# Revit family: RN 81124 Optipress-Aquaplus-Übergang
name_source: partatom
category: Rohrformteile
units: mm (PartAtom-declared; Revit-internal decimal feet)

## family parameters
Arbeitsebenenbasiert = Nein
Beim Laden mit Abzugskörper schneiden = Nein
Bemaßung runder Anschluss = Durchmesser verwenden
Gemeinsam genutzt = Nein
Immer vertikal = Ja
Teiletyp = Verbindung

## types (10) — shared parameters
1.010.00.2 Blattnummer der Richtlinie = 29
1.010.00.3 Ausgabedatum (Monat) der Richtlinie = 201308
1.010.00.4 Herstellername = R. Nussbaum AG
1.010.00.5 Revisionsdatum der Datei = 20190521
1.010.00.6 Webadresse des Herstellers = http://www.nussbaum.ch
1.100.00.4 Produktbezeichnung = Versorgung
1.110.00.2 Index = 4
1.110.00.4 Produktbezeichnung = Optipress
1.960/3L.00.8 Link (URL) = https://www.nussbaum.ch
29.700.00.4 Produktname = Optipress-Aquaplus-Übergang, auf alte Kupferrohre
29.700.00.5 Produktkennung = 2
29.700.00.6 Querschnittsform = 1
29.700.00.7 Nennweitensystem = DN
29.700.00.8 Nenndrucksystem = PN
29.710.02.4 Nenndruck = 16
29.710.02.5 max. zul. Überdruck [hPa] = 1600
29.710.02.7 max. zul. Dauer-Betriebsdruck [hPa] = 1600
29.710.02.9 max. zul. Dauer-Betriebstemperatur [°C] = 95
Connector Visibility = Nein
EnclosingSpace Visibility = Nein
Hersteller = R. Nussbaum AG
URL = https://www.nussbaum.ch

## per-type parameters (varying)
- DN=10x8: 1.800.00.3 TGA-Nummer=01900400000000000000000000000000000000000000000059000000000000000010; 1.800.00.4 Kommentarfeld=81124.20, Optipress-Aquaplus-Übergang, auf alte Kupferrohre, DN=10x8, L=40; 1.810.00.3 Hersteller-Bestellnummer=81124.2; 1.810.00.4 DATANORM-Nummer=81124.20; 1.810.00.6 GTIN-Nummer=7612945713940; 29.710.02.10 Formstück-Gewicht [kg]=0.028; 29.710.02.3 Benennung=Optipress-Aquaplus-Übergang, auf alte Kupferrohre, DN=10x8, L=40; CONNECTOR0_DIAMETER_dX_0r=10 mm  [stored 0.0328084 ft]; CONNECTOR0_dX_01=18 mm; CONNECTOR0_ref_dX=18 mm; CONNECTOR1_DIAMETER_dX_0r=8 mm  [stored 0.0262467 ft]; CONNECTOR1_dX_00=22 mm; CONNECTOR1_dX_01=40 mm; CONNECTOR1_ref_dX=22 mm; Modell=81124.2; R. Nussbaum AG 81124.20 de Visibility=Ja; R. Nussbaum AG 81124.21 de Visibility=Nein; R. Nussbaum AG 81124.22 de Visibility=Nein; R. Nussbaum AG 81124.23 de Visibility=Nein; R. Nussbaum AG 81124.24 de Visibility=Nein; R. Nussbaum AG 81124.25 de Visibility=Nein; R. Nussbaum AG 81124.26 de Visibility=Nein; R. Nussbaum AG 81124.27 de Visibility=Nein; R. Nussbaum AG 81124.28 de Visibility=Nein; R. Nussbaum AG 81124.29 de Visibility=Nein; Typenkommentare=Optipress-Aquaplus-Übergang DN=10x8
- DN=10: 1.800.00.3 TGA-Nummer=01900400000000000000000000000000000000000000000059000000000000000009; 1.800.00.4 Kommentarfeld=81124.29, Optipress-Aquaplus-Übergang, auf alte Kupferrohre, DN=10, L=40; 1.810.00.3 Hersteller-Bestellnummer=81124.29; 1.810.00.4 DATANORM-Nummer=81124.29; 1.810.00.6 GTIN-Nummer=7612945742407; 29.710.02.10 Formstück-Gewicht [kg]=0.029; 29.710.02.3 Benennung=Optipress-Aquaplus-Übergang, auf alte Kupferrohre, DN=10, L=40; CONNECTOR0_DIAMETER_dX_0r=10 mm  [stored 0.0328084 ft]; CONNECTOR0_dX_01=18 mm; CONNECTOR0_ref_dX=18 mm; CONNECTOR1_DIAMETER_dX_0r=10 mm  [stored 0.0328084 ft]; CONNECTOR1_dX_00=22 mm; CONNECTOR1_dX_01=40 mm; CONNECTOR1_ref_dX=22 mm; Modell=81124.29; R. Nussbaum AG 81124.20 de Visibility=Nein; R. Nussbaum AG 81124.21 de Visibility=Nein; R. Nussbaum AG 81124.22 de Visibility=Nein; R. Nussbaum AG 81124.23 de Visibility=Nein; R. Nussbaum AG 81124.24 de Visibility=Nein; R. Nussbaum AG 81124.25 de Visibility=Nein; R. Nussbaum AG 81124.26 de Visibility=Nein; R. Nussbaum AG 81124.27 de Visibility=Nein; R. Nussbaum AG 81124.28 de Visibility=Nein; R. Nussbaum AG 81124.29 de Visibility=Ja; Typenkommentare=Optipress-Aquaplus-Übergang DN=10
- DN=25: 1.800.00.3 TGA-Nummer=01900400000000000000000000000000000000000000000059000000000000000008; 1.800.00.4 Kommentarfeld=81124.28, Optipress-Aquaplus-Übergang, auf alte Kupferrohre, DN=25, L=58; 1.810.00.3 Hersteller-Bestellnummer=81124.28; 1.810.00.4 DATANORM-Nummer=81124.28; 1.810.00.5 StLB-Nummer=265.115; 1.810.00.6 GTIN-Nummer=7612945723550; 29.710.02.10 Formstück-Gewicht [kg]=0.097; 29.710.02.3 Benennung=Optipress-Aquaplus-Übergang, auf alte Kupferrohre, DN=25, L=58; CONNECTOR0_DIAMETER_dX_0r=25 mm  [stored 0.082021 ft]; CONNECTOR0_dX_01=24 mm; CONNECTOR0_ref_dX=24 mm; CONNECTOR1_DIAMETER_dX_0r=25 mm  [stored 0.082021 ft]; CONNECTOR1_dX_00=34 mm; CONNECTOR1_dX_01=58 mm; CONNECTOR1_ref_dX=34 mm; Modell=81124.28; R. Nussbaum AG 81124.20 de Visibility=Nein; R. Nussbaum AG 81124.21 de Visibility=Nein; R. Nussbaum AG 81124.22 de Visibility=Nein; R. Nussbaum AG 81124.23 de Visibility=Nein; R. Nussbaum AG 81124.24 de Visibility=Nein; R. Nussbaum AG 81124.25 de Visibility=Nein; R. Nussbaum AG 81124.26 de Visibility=Nein; R. Nussbaum AG 81124.27 de Visibility=Nein; R. Nussbaum AG 81124.28 de Visibility=Ja; R. Nussbaum AG 81124.29 de Visibility=Nein; Typenkommentare=Optipress-Aquaplus-Übergang DN=25
- DN=20: 1.800.00.3 TGA-Nummer=01900400000000000000000000000000000000000000000059000000000000000007; 1.800.00.4 Kommentarfeld=81124.27, Optipress-Aquaplus-Übergang, auf alte Kupferrohre, DN=20, L=55; 1.810.00.3 Hersteller-Bestellnummer=81124.27; 1.810.00.4 DATANORM-Nummer=81124.27; 1.810.00.5 StLB-Nummer=265.114; 1.810.00.6 GTIN-Nummer=7612945723543; 29.710.02.10 Formstück-Gewicht [kg]=0.074; 29.710.02.3 Benennung=Optipress-Aquaplus-Übergang, auf alte Kupferrohre, DN=20, L=55; CONNECTOR0_DIAMETER_dX_0r=20 mm; CONNECTOR0_dX_01=24 mm; CONNECTOR0_ref_dX=24 mm; CONNECTOR1_DIAMETER_dX_0r=20 mm; CONNECTOR1_dX_00=31 mm; CONNECTOR1_dX_01=55 mm; CONNECTOR1_ref_dX=31 mm; Modell=81124.27; R. Nussbaum AG 81124.20 de Visibility=Nein; R. Nussbaum AG 81124.21 de Visibility=Nein; R. Nussbaum AG 81124.22 de Visibility=Nein; R. Nussbaum AG 81124.23 de Visibility=Nein; R. Nussbaum AG 81124.24 de Visibility=Nein; R. Nussbaum AG 81124.25 de Visibility=Nein; R. Nussbaum AG 81124.26 de Visibility=Nein; R. Nussbaum AG 81124.27 de Visibility=Ja; R. Nussbaum AG 81124.28 de Visibility=Nein; R. Nussbaum AG 81124.29 de Visibility=Nein; Typenkommentare=Optipress-Aquaplus-Übergang DN=20
- DN=2: 1.800.00.3 TGA-Nummer=01900400000000000000000000000000000000000000000059000000000000000006; 1.800.00.4 Kommentarfeld=81124.26, Optipress-Aquaplus-Übergang, auf alte Kupferrohre, DN=15, L=52; 1.810.00.3 Hersteller-Bestellnummer=81124.26; 1.810.00.4 DATANORM-Nummer=81124.26; 1.810.00.5 StLB-Nummer=265.113; 1.810.00.6 GTIN-Nummer=7612945723536; 29.710.02.10 Formstück-Gewicht [kg]=0.058; 29.710.02.3 Benennung=Optipress-Aquaplus-Übergang, auf alte Kupferrohre, DN=15, L=52; CONNECTOR0_DIAMETER_dX_0r=15 mm; CONNECTOR0_dX_01=22 mm; CONNECTOR0_ref_dX=22 mm; CONNECTOR1_DIAMETER_dX_0r=15 mm; CONNECTOR1_dX_00=30 mm; CONNECTOR1_dX_01=52 mm; CONNECTOR1_ref_dX=30 mm; Modell=81124.26; R. Nussbaum AG 81124.20 de Visibility=Nein; R. Nussbaum AG 81124.21 de Visibility=Nein; R. Nussbaum AG 81124.22 de Visibility=Nein; R. Nussbaum AG 81124.23 de Visibility=Nein; R. Nussbaum AG 81124.24 de Visibility=Nein; R. Nussbaum AG 81124.25 de Visibility=Nein; R. Nussbaum AG 81124.26 de Visibility=Ja; R. Nussbaum AG 81124.27 de Visibility=Nein; R. Nussbaum AG 81124.28 de Visibility=Nein; R. Nussbaum AG 81124.29 de Visibility=Nein; Typenkommentare=Optipress-Aquaplus-Übergang DN=15
- DN=1: 1.800.00.3 TGA-Nummer=01900400000000000000000000000000000000000000000059000000000000000005; 1.800.00.4 Kommentarfeld=81124.25, Optipress-Aquaplus-Übergang, auf alte Kupferrohre, DN=12, L=51; 1.810.00.3 Hersteller-Bestellnummer=81124.25; 1.810.00.4 DATANORM-Nummer=81124.25; 1.810.00.5 StLB-Nummer=265.112; 1.810.00.6 GTIN-Nummer=7612945723529; 29.710.02.10 Formstück-Gewicht [kg]=0.048; 29.710.02.3 Benennung=Optipress-Aquaplus-Übergang, auf alte Kupferrohre, DN=12, L=51; CONNECTOR0_DIAMETER_dX_0r=12 mm  [stored 0.0393701 ft]; CONNECTOR0_dX_01=22 mm; CONNECTOR0_ref_dX=22 mm; CONNECTOR1_DIAMETER_dX_0r=12 mm  [stored 0.0393701 ft]; CONNECTOR1_dX_00=29 mm; CONNECTOR1_dX_01=51 mm; CONNECTOR1_ref_dX=29 mm; Modell=81124.25; R. Nussbaum AG 81124.20 de Visibility=Nein; R. Nussbaum AG 81124.21 de Visibility=Nein; R. Nussbaum AG 81124.22 de Visibility=Nein; R. Nussbaum AG 81124.23 de Visibility=Nein; R. Nussbaum AG 81124.24 de Visibility=Nein; R. Nussbaum AG 81124.25 de Visibility=Ja; R. Nussbaum AG 81124.26 de Visibility=Nein; R. Nussbaum AG 81124.27 de Visibility=Nein; R. Nussbaum AG 81124.28 de Visibility=Nein; R. Nussbaum AG 81124.29 de Visibility=Nein; Typenkommentare=Optipress-Aquaplus-Übergang DN=12
- DN=15: 1.800.00.3 TGA-Nummer=01900400000000000000000000000000000000000000000059000000000000000004; 1.800.00.4 Kommentarfeld=81124.24, Optipress-Aquaplus-Übergang, auf alte Kupferrohre, DN=15, L=52; 1.810.00.3 Hersteller-Bestellnummer=81124.24; 1.810.00.4 DATANORM-Nummer=81124.24; 1.810.00.5 StLB-Nummer=265.213; 1.810.00.6 GTIN-Nummer=7612945694218; 29.710.02.10 Formstück-Gewicht [kg]=0.065; 29.710.02.3 Benennung=Optipress-Aquaplus-Übergang, auf alte Kupferrohre, DN=15, L=52; CONNECTOR0_DIAMETER_dX_0r=15 mm; CONNECTOR0_dX_01=22 mm; CONNECTOR0_ref_dX=22 mm; CONNECTOR1_DIAMETER_dX_0r=15 mm; CONNECTOR1_dX_00=30 mm; CONNECTOR1_dX_01=52 mm; CONNECTOR1_ref_dX=30 mm; Modell=81124.24; R. Nussbaum AG 81124.20 de Visibility=Nein; R. Nussbaum AG 81124.21 de Visibility=Nein; R. Nussbaum AG 81124.22 de Visibility=Nein; R. Nussbaum AG 81124.23 de Visibility=Nein; R. Nussbaum AG 81124.24 de Visibility=Ja; R. Nussbaum AG 81124.25 de Visibility=Nein; R. Nussbaum AG 81124.26 de Visibility=Nein; R. Nussbaum AG 81124.27 de Visibility=Nein; R. Nussbaum AG 81124.28 de Visibility=Nein; R. Nussbaum AG 81124.29 de Visibility=Nein; Typenkommentare=Optipress-Aquaplus-Übergang DN=15
- DN=12: 1.800.00.3 TGA-Nummer=01900400000000000000000000000000000000000000000059000000000000000003; 1.800.00.4 Kommentarfeld=81124.23, Optipress-Aquaplus-Übergang, auf alte Kupferrohre, DN=12, L=52; 1.810.00.3 Hersteller-Bestellnummer=81124.23; 1.810.00.4 DATANORM-Nummer=81124.23; 1.810.00.5 StLB-Nummer=265.212; 1.810.00.6 GTIN-Nummer=7612945688477; 29.710.02.10 Formstück-Gewicht [kg]=0.06; 29.710.02.3 Benennung=Optipress-Aquaplus-Übergang, auf alte Kupferrohre, DN=12, L=52; CONNECTOR0_DIAMETER_dX_0r=12 mm  [stored 0.0393701 ft]; CONNECTOR0_dX_01=22 mm; CONNECTOR0_ref_dX=22 mm; CONNECTOR1_DIAMETER_dX_0r=12 mm  [stored 0.0393701 ft]; CONNECTOR1_dX_00=30 mm; CONNECTOR1_dX_01=52 mm; CONNECTOR1_ref_dX=30 mm; Modell=81124.23; R. Nussbaum AG 81124.20 de Visibility=Nein; R. Nussbaum AG 81124.21 de Visibility=Nein; R. Nussbaum AG 81124.22 de Visibility=Nein; R. Nussbaum AG 81124.23 de Visibility=Ja; R. Nussbaum AG 81124.24 de Visibility=Nein; R. Nussbaum AG 81124.25 de Visibility=Nein; R. Nussbaum AG 81124.26 de Visibility=Nein; R. Nussbaum AG 81124.27 de Visibility=Nein; R. Nussbaum AG 81124.28 de Visibility=Nein; R. Nussbaum AG 81124.29 de Visibility=Nein; Typenkommentare=Optipress-Aquaplus-Übergang DN=12
- DN=15x10: 1.800.00.3 TGA-Nummer=01900400000000000000000000000000000000000000000059000000000000000002; 1.800.00.4 Kommentarfeld=81124.22, Optipress-Aquaplus-Übergang, auf alte Kupferrohre, DN=15x10, L=45; 1.810.00.3 Hersteller-Bestellnummer=81124.22; 1.810.00.4 DATANORM-Nummer=81124.22; 1.810.00.6 GTIN-Nummer=7612945714053; 29.710.02.10 Formstück-Gewicht [kg]=0.045; 29.710.02.3 Benennung=Optipress-Aquaplus-Übergang, auf alte Kupferrohre, DN=15x10, L=45; CONNECTOR0_DIAMETER_dX_0r=15 mm; CONNECTOR0_dX_01=22 mm; CONNECTOR0_ref_dX=22 mm; CONNECTOR1_DIAMETER_dX_0r=10 mm  [stored 0.0328084 ft]; CONNECTOR1_dX_00=27 mm; CONNECTOR1_dX_01=45 mm; CONNECTOR1_ref_dX=27 mm; Modell=81124.22; R. Nussbaum AG 81124.20 de Visibility=Nein; R. Nussbaum AG 81124.21 de Visibility=Nein; R. Nussbaum AG 81124.22 de Visibility=Ja; R. Nussbaum AG 81124.23 de Visibility=Nein; R. Nussbaum AG 81124.24 de Visibility=Nein; R. Nussbaum AG 81124.25 de Visibility=Nein; R. Nussbaum AG 81124.26 de Visibility=Nein; R. Nussbaum AG 81124.27 de Visibility=Nein; R. Nussbaum AG 81124.28 de Visibility=Nein; R. Nussbaum AG 81124.29 de Visibility=Nein; Typenkommentare=Optipress-Aquaplus-Übergang DN=15x10
- DN=15x8: 1.800.00.3 TGA-Nummer=01900400000000000000000000000000000000000000000059000000000000000001; 1.800.00.4 Kommentarfeld=81124.21, Optipress-Aquaplus-Übergang, auf alte Kupferrohre, DN=15x8, L=46; 1.810.00.3 Hersteller-Bestellnummer=81124.21; 1.810.00.4 DATANORM-Nummer=81124.21; 1.810.00.6 GTIN-Nummer=7612945713957; 29.710.02.10 Formstück-Gewicht [kg]=0.034; 29.710.02.3 Benennung=Optipress-Aquaplus-Übergang, auf alte Kupferrohre, DN=15x8, L=46; CONNECTOR0_DIAMETER_dX_0r=15 mm; CONNECTOR0_dX_01=22 mm; CONNECTOR0_ref_dX=22 mm; CONNECTOR1_DIAMETER_dX_0r=8 mm  [stored 0.0262467 ft]; CONNECTOR1_dX_00=28 mm; CONNECTOR1_dX_01=46 mm; CONNECTOR1_ref_dX=28 mm; Modell=81124.21; R. Nussbaum AG 81124.20 de Visibility=Nein; R. Nussbaum AG 81124.21 de Visibility=Ja; R. Nussbaum AG 81124.22 de Visibility=Nein; R. Nussbaum AG 81124.23 de Visibility=Nein; R. Nussbaum AG 81124.24 de Visibility=Nein; R. Nussbaum AG 81124.25 de Visibility=Nein; R. Nussbaum AG 81124.26 de Visibility=Nein; R. Nussbaum AG 81124.27 de Visibility=Nein; R. Nussbaum AG 81124.28 de Visibility=Nein; R. Nussbaum AG 81124.29 de Visibility=Nein; Typenkommentare=Optipress-Aquaplus-Übergang DN=15x8

note: [stored X ft] marks values corroborated as IEEE doubles in the binary element streams (Revit-internal decimal feet)

## geometry (parser evidence)
native form markers: Sweep x1
no freeform markers — native parametric forms only
